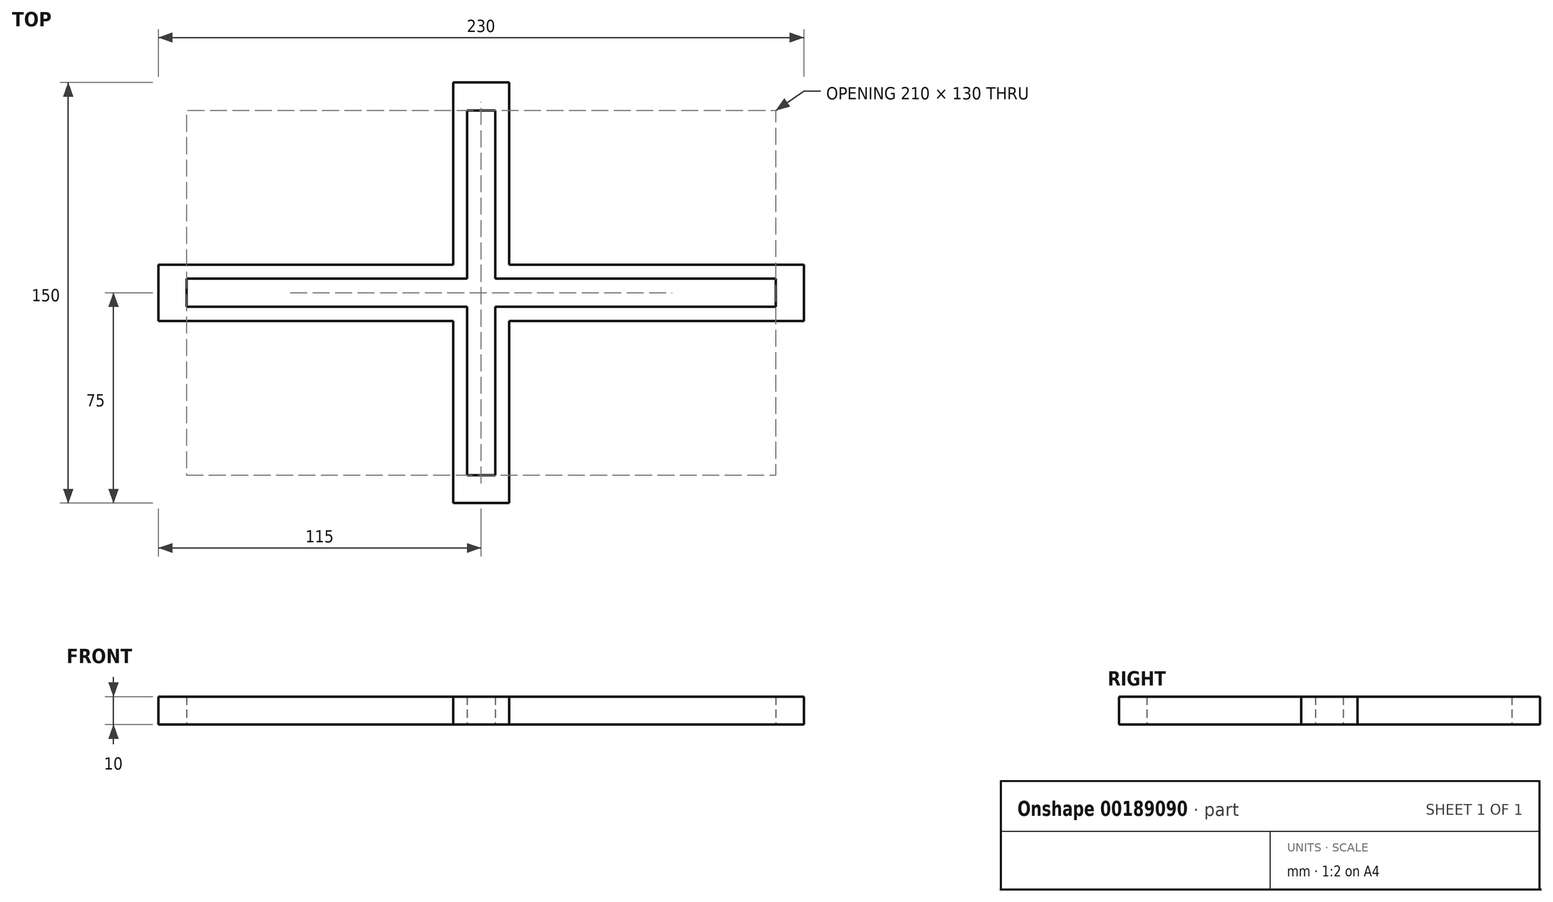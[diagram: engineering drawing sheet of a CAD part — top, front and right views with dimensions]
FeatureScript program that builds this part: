
annotation { "Feature Type Name" : "Feature", "Feature Type Description" : "" }
export const myFeature = defineFeature(function(context is Context, id is Id, definition is map)
    precondition{}
    {
        {
            var Q0;
            Q0=qCreatedBy(makeId("Top.planeOp"),FACE);
            var sketch = newSketch(context, id + "F0", { "sketchPlane" : qUnion([Q0])});
            skLineSegment(sketch, "E0.bottom", {"start": v(-115, 10) * mm, "end": v(115, 10) * mm});
            skLineSegment(sketch, "E0.top", {"start": v(-115, -10) * mm, "end": v(115, -10) * mm});
            skLineSegment(sketch, "E0.left", {"start": v(-115, 10) * mm, "end": v(-115, -10) * mm});
            skLineSegment(sketch, "E0.right", {"start": v(115, 10) * mm, "end": v(115, -10) * mm});
            skPoint(sketch, "E0.middle", {"position": v(0, 0) * mm});
            skLineSegment(sketch, "E1.bottom", {"start": v(10, -75) * mm, "end": v(-10, -75) * mm});
            skLineSegment(sketch, "E1.top", {"start": v(10, 75) * mm, "end": v(-10, 75) * mm});
            skLineSegment(sketch, "E1.left", {"start": v(10, -75) * mm, "end": v(10, 75) * mm});
            skLineSegment(sketch, "E1.right", {"start": v(-10, -75) * mm, "end": v(-10, 75) * mm});
            skLineSegment(sketch, "E2.bottom", {"start": v(-5, 65) * mm, "end": v(5, 65) * mm});
            skLineSegment(sketch, "E2.top", {"start": v(-5, -65) * mm, "end": v(5, -65) * mm});
            skLineSegment(sketch, "E2.left", {"start": v(-5, 65) * mm, "end": v(-5, -65) * mm});
            skLineSegment(sketch, "E2.right", {"start": v(5, 65) * mm, "end": v(5, -65) * mm});
            skLineSegment(sketch, "E3.bottom", {"start": v(105, 5) * mm, "end": v(-105, 5) * mm});
            skLineSegment(sketch, "E3.top", {"start": v(105, -5) * mm, "end": v(-105, -5) * mm});
            skLineSegment(sketch, "E3.left", {"start": v(105, 5) * mm, "end": v(105, -5) * mm});
            skLineSegment(sketch, "E3.right", {"start": v(-105, 5) * mm, "end": v(-105, -5) * mm});
            skSolve(sketch);
        }
        {
            var Q0;
            Q0 = qSketchRegion(id + "F0", true);
            extrude(context, id + "F1", {"entities" : qUnion([Q0]), "depth" : 10 * mm});
        }
    });
